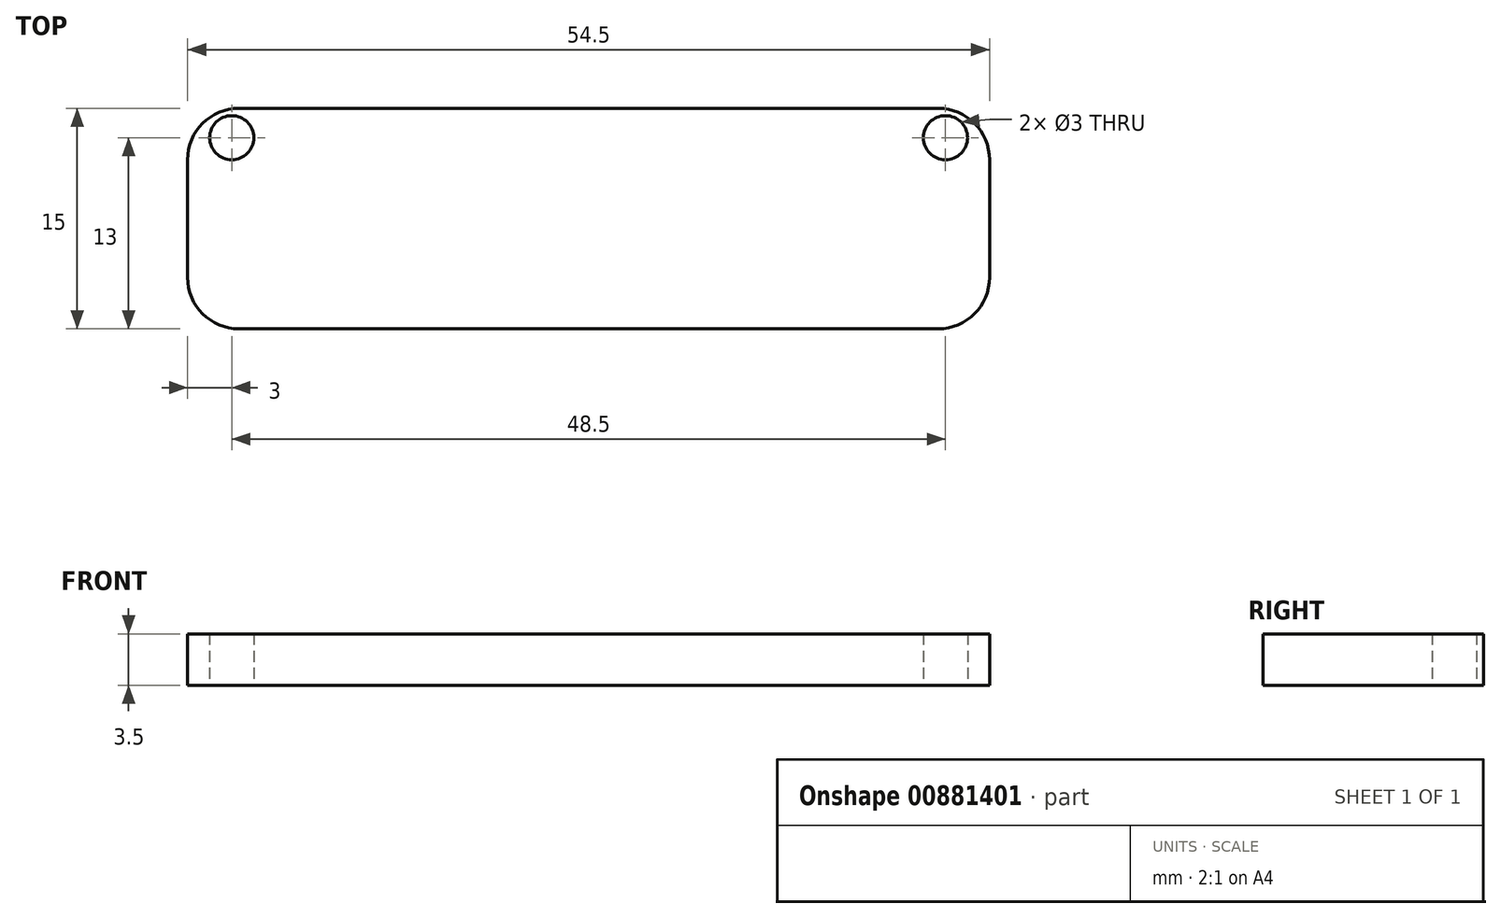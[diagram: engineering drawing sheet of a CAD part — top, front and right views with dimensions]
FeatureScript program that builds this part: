
annotation { "Feature Type Name" : "Feature", "Feature Type Description" : "" }
export const myFeature = defineFeature(function(context is Context, id is Id, definition is map)
    precondition{}
    {
        {
            var Q0;
            Q0=qCreatedBy(makeId("Top.planeOp"),FACE);
            var sketch = newSketch(context, id + "F0", { "sketchPlane" : qUnion([Q0])});
            skLineSegment(sketch, "E0.bottom", {"start": v(33, -7.5) * mm, "end": v(-33, -7.5) * mm});
            skLineSegment(sketch, "E0.top", {"start": v(33, 7.5) * mm, "end": v(-33, 7.5) * mm});
            skLineSegment(sketch, "E0.left", {"start": v(33, -7.5) * mm, "end": v(33, 7.5) * mm});
            skLineSegment(sketch, "E0.right", {"start": v(-33, -7.5) * mm, "end": v(-33, 7.5) * mm});
            skPoint(sketch, "E0.middle", {"position": v(0, 0) * mm});
            skPoint(sketch, "E1", {"position": v(27.25, -7.5) * mm});
            skPoint(sketch, "E2", {"position": v(-27.25, -7.5) * mm});
            skPoint(sketch, "E3", {"position": v(-27.25, -22.5) * mm});
            skPoint(sketch, "E4", {"position": v(27.25, -22.5) * mm});
            skLineSegment(sketch, "E5", {"start": v(-27.25, -7.5) * mm, "end": v(-27.25, -22.5) * mm});
            skLineSegment(sketch, "E6", {"start": v(-27.25, -22.5) * mm, "end": v(27.25, -22.5) * mm});
            skLineSegment(sketch, "E7", {"start": v(27.25, -22.5) * mm, "end": v(27.25, -7.5) * mm});
            skPoint(sketch, "E8", {"position": v(-30, -3.5) * mm});
            skPoint(sketch, "E9", {"position": v(30, -3.5) * mm});
            skPoint(sketch, "E10", {"position": v(-24.25, -9.5) * mm});
            skPoint(sketch, "E11", {"position": v(24.25, -9.5) * mm});
            skCircle(sketch, "E12", {"center": v(-30, -3.5) * mm, "radius": 1.5 * mm});
            skCircle(sketch, "E13", {"center": v(30, -3.5) * mm, "radius": 1.5 * mm});
            skCircle(sketch, "E14", {"center": v(-24.25, -9.5) * mm, "radius": 1.5 * mm});
            skCircle(sketch, "E15", {"center": v(24.25, -9.5) * mm, "radius": 1.5 * mm});
            skSolve(sketch);
        }
        {
            var Q0;
            Q0=makeQuery(id+"F0.imprint","IMPRINT",FACE,{"disambiguationData":[TD([[makeQuery(id+"F0.imprint","IMPRINT",EDGE,{"derivedFrom":sQuery(id+"F0.wireOp",EDGE,"E0.top")}),1.0]])]});
            var Q1;
            {var subQ1=sQuery(id+"F0.wireOp",EDGE,"E5");Q1=makeQuery(id+"F0.imprint","IMPRINT",FACE,{"disambiguationData":[TD([[makeQuery(id+"F0.imprint","IMPRINT",EDGE,{"derivedFrom":subQ1}),1.0]])]});}
            extrude(context, id + "F1", {"entities" : qUnion([Q0, Q1]), "depth" : 3.5 * mm, "offsetDistance" : 25 * mm});
        }
        {
            var Q0;
            Q0=makeQuery(id+"F1.opExtrude","SWEPT_EDGE",EDGE,{"disambiguationData":[OSD([sQuery(id+"F0.wireOp",EDGE,"E0.top"),sQuery(id+"F0.wireOp",EDGE,"E0.right")])]});
            var Q1;
            Q1=makeQuery(id+"F1.opExtrude","SWEPT_EDGE",EDGE,{"disambiguationData":[OSD([sQuery(id+"F0.wireOp",EDGE,"E0.top"),sQuery(id+"F0.wireOp",EDGE,"E0.left")])]});
            var Q2;
            Q2=makeQuery(id+"F1.opExtrude","SWEPT_EDGE",EDGE,{"disambiguationData":[OSD([sQuery(id+"F0.wireOp",EDGE,"E6"),sQuery(id+"F0.wireOp",EDGE,"E7")])]});
            var Q3;
            Q3=makeQuery(id+"F1.opExtrude","SWEPT_EDGE",EDGE,{"disambiguationData":[OSD([sQuery(id+"F0.wireOp",EDGE,"E5"),sQuery(id+"F0.wireOp",EDGE,"E6")])]});
            var Q4;
            Q4=makeQuery(id+"F1.opExtrude","SWEPT_EDGE",EDGE,{"disambiguationData":[OSD([sQuery(id+"F0.wireOp",EDGE,"E0.bottom"),sQuery(id+"F0.wireOp",EDGE,"E0.left")])]});
            var Q5;
            Q5=makeQuery(id+"F1.opExtrude","SWEPT_EDGE",EDGE,{"disambiguationData":[OSD([sQuery(id+"F0.wireOp",EDGE,"E0.bottom"),sQuery(id+"F0.wireOp",EDGE,"E0.right")])]});
            fillet(context, id + "F2", {"entities" : qUnion([Q0, Q1, Q2, Q3, Q4, Q5]), "tangentPropagation" : true, "radius" : 3.5 * mm, "defaultsChanged" : true, "vertexSettings" : [], "allowEdgeOverflow" : false});
        }
    });
